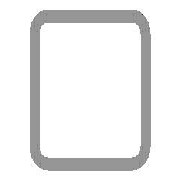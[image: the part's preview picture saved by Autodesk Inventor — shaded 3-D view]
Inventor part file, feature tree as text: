
AUTODESK INVENTOR PART (.ipt)
format: ipt  version: 2025 (Build 290162010, 162A)  size: 271,872 bytes
history: native  units: mm (DEFAULTED — no unit token found)
features: sketch x8, extrude x4, other x3, hole x3, fillet x2, plane x1, projected_geometry x1
ambient origin geometry x8: Origin, YZ Plane, XZ Plane, XY Plane, X Axis, Y Axis, Z Axis, Center Point
bodies: Solid1 (feature_tree)
feature tree (22):
  other  "Driven Length"
  other  "Startebene"
  other  "Endebene"
  extrude  "Körper"  TaperAngle=0.0deg  [1 undecoded]
  extrude  "Extrusion2"  Depth=20.0mm
  hole  "Bohrung5"  [1 undecoded]
  hole  "Bohrung7"  [1 undecoded]
  sketch  "Skizze13"  dims[d17=90.0deg d18=200.0mm]
  extrude  "Extrusion3"  Depth=10.0mm
  extrude  "Extrusion4"  Depth=200.0mm
  hole  "Bohrung6"  [1 undecoded]
  fillet  "Rundung3"  [1 undecoded]
  fillet  "Rundung4"  Radius=16.0mm
  sketch  "Sketch3"  dims[d3=200.0mm d4=0.0mm]
  plane  "Work Plane3"
  sketch  "Skizze9"  dims[d7=3.0mm d10=20.0mm]
  sketch  "Skizze10"  dims[d11=20.0mm d12=2.0mm]
  sketch  "Skizze11"  dims[d13=-0.0mm d14=200.0mm]
  sketch  "Skizze12"  dims[d15=10.0mm d16=10.0mm]
  sketch  "Skizze14"  dims[d47=6.0mm d48=35.0mm d49=0.0mm d50=0.0mm d51=16.0mm]
  projected_geometry  "Projizierte Kontur1"
  sketch  "Skizze15"  dims[d52=2.459mm d53=50.0mm d54=4.0mm d55=2.0mm d56=90.0deg d57=7.8mm d58=20.594885mm d59=5.0mm d60=3.0mm d61=5.0mm d62=4.0mm d63=2.0mm d64=90.0deg d65=6.3mm d66=20.594885mm d67=110.0mm d68=3.2mm d69=6.0mm d70=6.3mm d71=2.0mm d72=90.0deg d73=8.0mm d74=20.594885mm d75=30.0mm d76=0.0mm d77=30.0mm d78=0.0mm d79=0.0mm d80=1.0mm d81=1.0mm]
note: 5 required parameter values undecoded (feature->parameter linkage not recoverable at this tier; creation-order binding heuristic only, values carry confidence <= 0.55)
